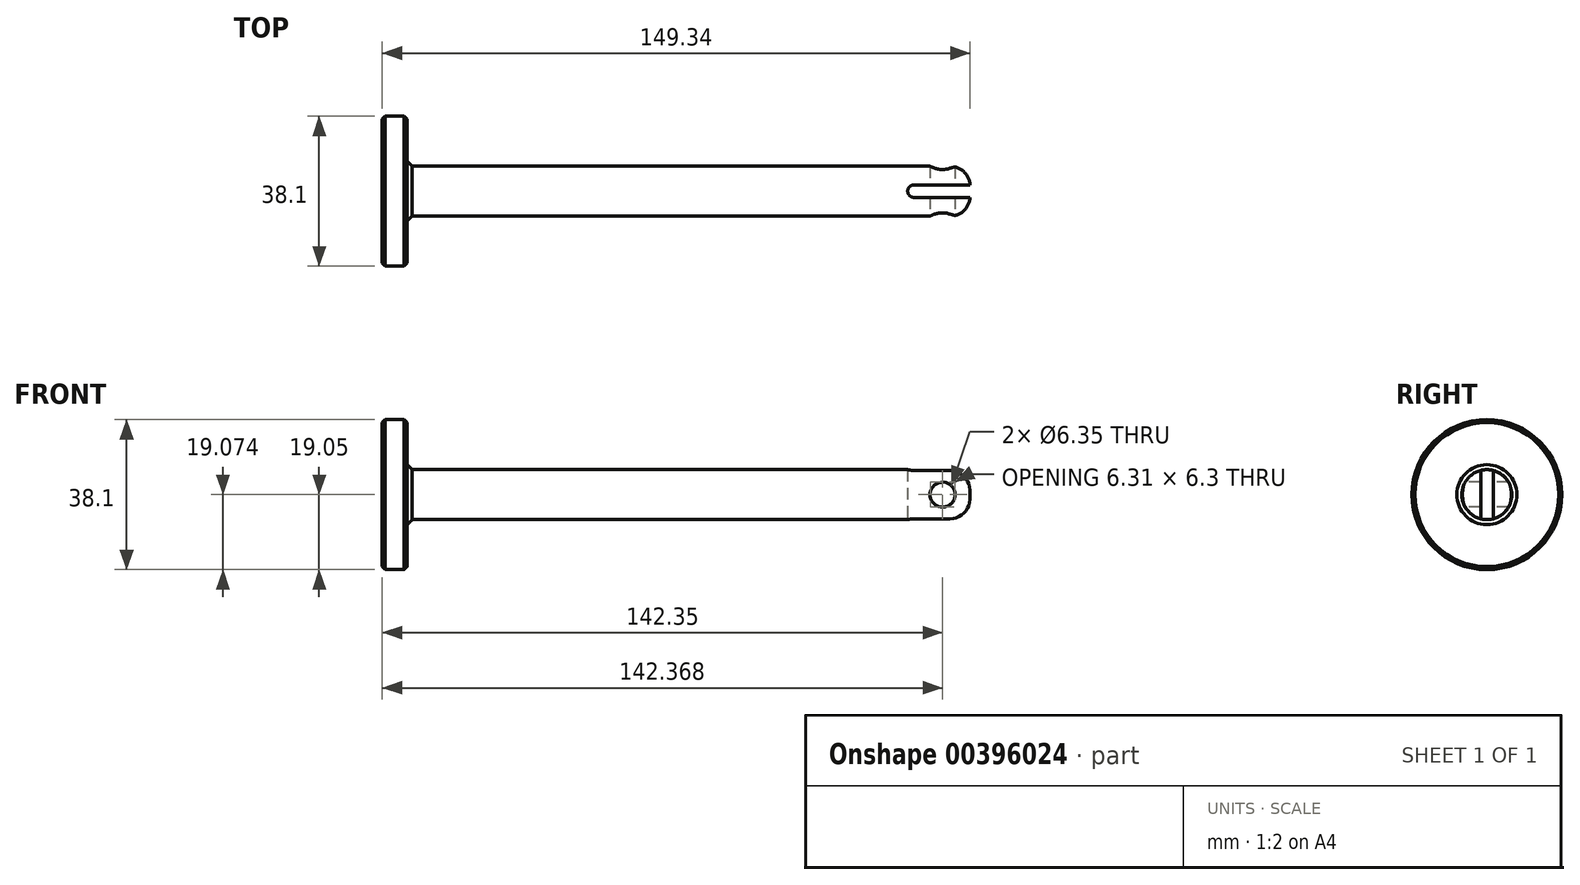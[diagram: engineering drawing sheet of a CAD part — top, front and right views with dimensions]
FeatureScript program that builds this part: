
annotation { "Feature Type Name" : "Feature", "Feature Type Description" : "" }
export const myFeature = defineFeature(function(context is Context, id is Id, definition is map)
    precondition{}
    {
        {
            var Q0;
            Q0=qCreatedBy(makeId("Front.planeOp"),FACE);
            var sketch = newSketch(context, id + "F0", { "sketchPlane" : qUnion([Q0])});
            skLineSegment(sketch, "E0.bottom", {"start": v(-6.35, 19.05) * mm, "end": v(0, 19.05) * mm});
            skLineSegment(sketch, "E0.left", {"start": v(-6.35, 19.05) * mm, "end": v(-6.35, 0) * mm});
            skLineSegment(sketch, "E0.right", {"start": v(0, 19.05) * mm, "end": v(0, 0) * mm});
            skLineSegment(sketch, "E1", {"start": v(0, 0) * mm, "end": v(-6.35, 0) * mm});
            skLineSegment(sketch, "E2.bottom", {"start": v(0, 0) * mm, "end": v(143, 0) * mm});
            skLineSegment(sketch, "E2.top", {"start": v(0, 6.35) * mm, "end": v(143, 6.35) * mm});
            skLineSegment(sketch, "E2.right", {"start": v(143, 0) * mm, "end": v(143, 6.35) * mm});
            skPoint(sketch, "E3.orphan", {"position": v(85.72, 0) * mm});
            skSolve(sketch);
        }
        {
            var Q0;
            Q0 = qSketchRegion(id + "F0", true);
            var Q1;
            Q1=sQuery(id+"F0.wireOp",EDGE,"E2.bottom");
            revolve(context, id + "F1", {"surfaceOperationType" : NewSurfaceOperationType.NEW, "entities" : qUnion([Q0]), "axis" : qUnion([Q1]), "revolveType" : RevolveType.FULL});
        }
        {
            var Q0;
            Q0=makeQuery(id+"F1.opRevolve","SWEPT_EDGE",EDGE,{"disambiguationData":[OSD([sQuery(id+"F0.wireOp",EDGE,"E0.bottom"),sQuery(id+"F0.wireOp",EDGE,"E0.right")])]});
            var Q1;
            Q1=makeQuery(id+"F1.opRevolve","SWEPT_EDGE",EDGE,{"disambiguationData":[OSD([sQuery(id+"F0.wireOp",EDGE,"E0.bottom"),sQuery(id+"F0.wireOp",EDGE,"E0.left")])]});
            chamfer(context, id + "F2", {"entities" : qUnion([Q0, Q1]), "width" : 0.76 * mm, "tangentPropagation" : true});
        }
        {
            var Q0;
            Q0=makeQuery(id+"F1.opRevolve","SWEPT_EDGE",EDGE,{"disambiguationData":[OSD([sQuery(id+"F0.wireOp",EDGE,"E0.right"),sQuery(id+"F0.wireOp",EDGE,"E2.top")])]});
            chamfer(context, id + "F3", {"entities" : qUnion([Q0]), "width" : 1.27 * mm, "tangentPropagation" : true});
        }
        {
            var Q0;
            Q0=qCreatedBy(makeId("Front.planeOp"),FACE);
            var sketch = newSketch(context, id + "F4", { "sketchPlane" : qUnion([Q0])});
            skCircle(sketch, "E4", {"center": v(136, 0) * mm, "radius": 3.18 * mm});
            skSolve(sketch);
        }
        {
            var Q0;
            Q0 = qSketchRegion(id + "F4", true);
            extrude(context, id + "F5", {"entities" : qUnion([Q0]), "operationType" : NewBodyOperationType.REMOVE, "endBound" : BoundingType.SYMMETRIC, "oppositeDirection" : true, "depth" : 25.4 * mm, "offsetDistance" : 25.4 * mm});
        }
        {
            var Q0;
            Q0=qCreatedBy(makeId("Top.planeOp"),FACE);
            var sketch = newSketch(context, id + "F6", { "sketchPlane" : qUnion([Q0])});
            skLineSegment(sketch, "E5.bottom", {"start": v(143, 1.59) * mm, "end": v(127.13, 1.59) * mm});
            skLineSegment(sketch, "E5.top", {"start": v(143, -1.59) * mm, "end": v(127.13, -1.59) * mm});
            skLineSegment(sketch, "E5.left", {"start": v(143, 1.59) * mm, "end": v(143, -1.59) * mm});
            skLineSegment(sketch, "E5.right", {"start": v(127.13, 1.59) * mm, "end": v(127.13, -1.59) * mm});
            skSolve(sketch);
        }
        {
            var Q0;
            Q0 = qSketchRegion(id + "F6", true);
            extrude(context, id + "F7", {"entities" : qUnion([Q0]), "operationType" : NewBodyOperationType.REMOVE, "endBound" : BoundingType.SYMMETRIC, "oppositeDirection" : true, "depth" : 25.4 * mm, "offsetDistance" : 25.4 * mm});
        }
        {
            var Q0;
            Q0=makeQuery(id+"F7.boolean.opBoolean","COPY",EDGE,{"derivedFrom":makeQuery(id+"F7.opExtrude","SWEPT_EDGE",EDGE,{"disambiguationData":[OSD([sQuery(id+"F6.wireOp",EDGE,"E5.bottom"),sQuery(id+"F6.wireOp",EDGE,"E5.right")])]})});
            var Q1;
            Q1=makeQuery(id+"F7.boolean.opBoolean","COPY",EDGE,{"derivedFrom":makeQuery(id+"F7.opExtrude","SWEPT_EDGE",EDGE,{"disambiguationData":[OSD([sQuery(id+"F6.wireOp",EDGE,"E5.top"),sQuery(id+"F6.wireOp",EDGE,"E5.right")])]})});
            fillet(context, id + "F8", {"entities" : qUnion([Q0, Q1]), "radius" : 1.59 * mm, "tangentPropagation" : true, "allowEdgeOverflow" : false});
        }
        {
            var Q0;
            {var subQ0=sQuery(id+"F0.wireOp",EDGE,"E2.top");var subQ1=sQuery(id+"F0.wireOp",EDGE,"E2.right");Q0=makeQuery(id+"F7.boolean.opBoolean","SPLIT",EDGE,{"disambiguationData":[TD([makeQuery(id+"F7.opExtrude","SWEPT_FACE",FACE,{"disambiguationData":[OSD([sQuery(id+"F6.wireOp",EDGE,"E5.bottom")])]})])],"derivedFrom":makeQuery(id+"F1.opRevolve","SWEPT_EDGE",EDGE,{"disambiguationData":[OSD([subQ0,subQ1])]})});}
            var Q1;
            {var subQ0=sQuery(id+"F0.wireOp",EDGE,"E2.top");var subQ1=sQuery(id+"F0.wireOp",EDGE,"E2.right");Q1=makeQuery(id+"F7.boolean.opBoolean","SPLIT",EDGE,{"disambiguationData":[TD([makeQuery(id+"F7.opExtrude","SWEPT_FACE",FACE,{"disambiguationData":[OSD([sQuery(id+"F6.wireOp",EDGE,"E5.top")])]})])],"derivedFrom":makeQuery(id+"F1.opRevolve","SWEPT_EDGE",EDGE,{"disambiguationData":[OSD([subQ0,subQ1])]})});}
            fillet(context, id + "F9", {"entities" : qUnion([Q0, Q1]), "radius" : 5.08 * mm, "tangentPropagation" : true, "allowEdgeOverflow" : false});
        }
    });
